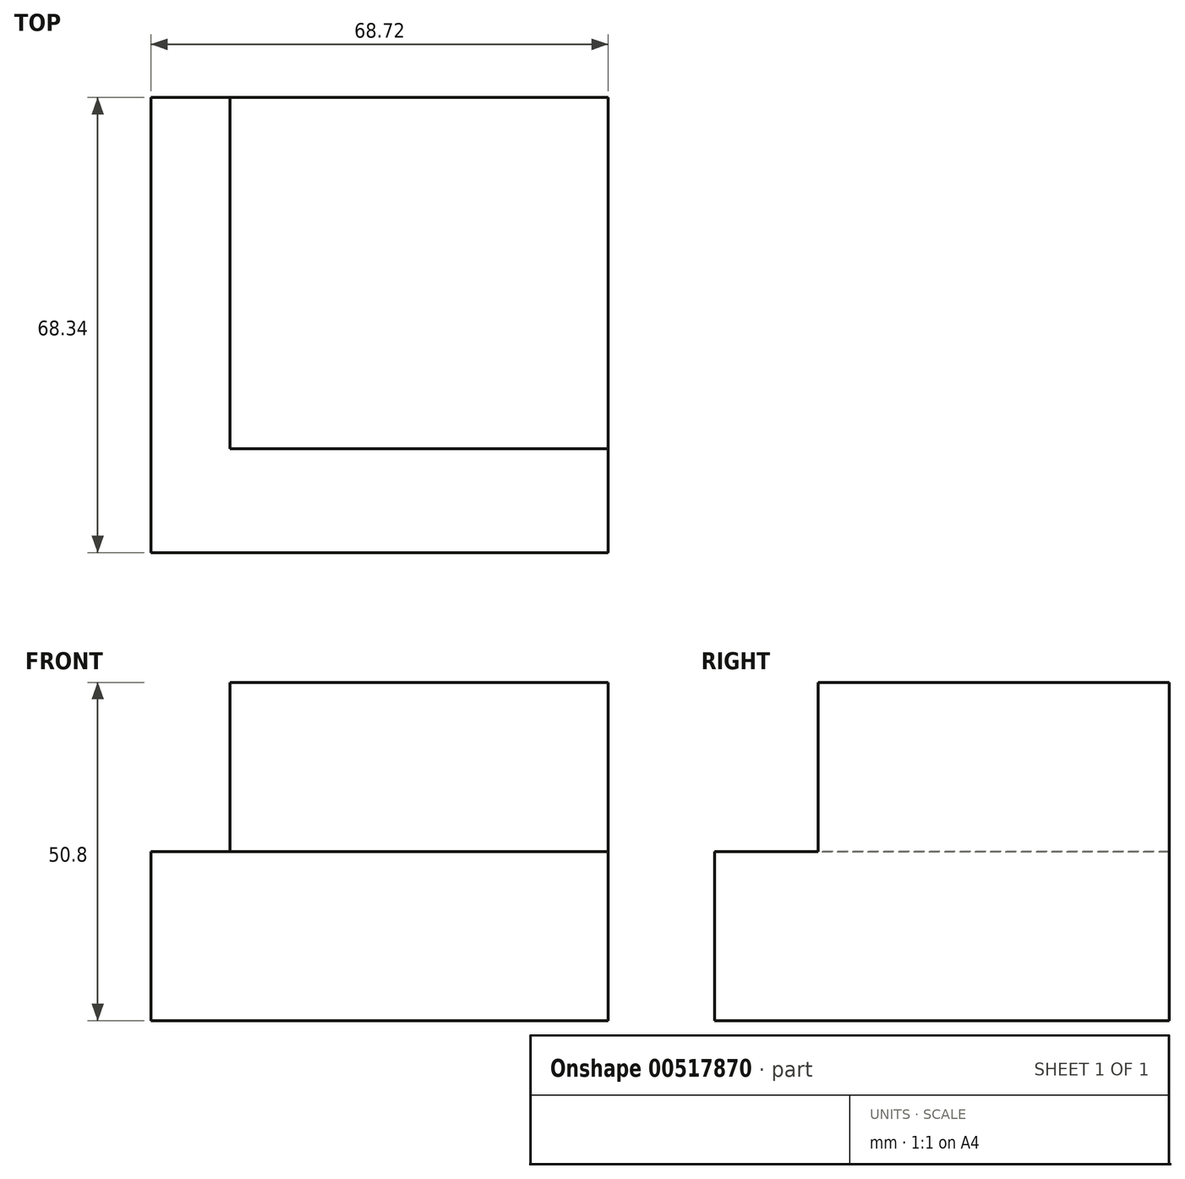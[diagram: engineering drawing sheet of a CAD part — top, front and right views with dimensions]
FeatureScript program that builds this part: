
annotation { "Feature Type Name" : "Feature", "Feature Type Description" : "" }
export const myFeature = defineFeature(function(context is Context, id is Id, definition is map)
    precondition{}
    {
        {
            var Q0;
            Q0=qCreatedBy(makeId("Top.planeOp"),FACE);
            var sketch = newSketch(context, id + "F0", { "sketchPlane" : qUnion([Q0])});
            skLineSegment(sketch, "E0.bottom", {"start": v(0, 0) * mm, "end": v(68.72, 0) * mm});
            skLineSegment(sketch, "E0.top", {"start": v(0, 68.34) * mm, "end": v(68.72, 68.34) * mm});
            skLineSegment(sketch, "E0.left", {"start": v(0, 0) * mm, "end": v(0, 68.34) * mm});
            skLineSegment(sketch, "E0.right", {"start": v(68.72, 0) * mm, "end": v(68.72, 68.34) * mm});
            skSolve(sketch);
        }
        {
            var Q0;
            Q0=makeQuery(id+"F0.imprint","IMPRINT",FACE,{"disambiguationData":[TD([[makeQuery(id+"F0.imprint","IMPRINT",EDGE,{"derivedFrom":sQuery(id+"F0.wireOp",EDGE,"E0.bottom")}),1.0]])]});
            extrude(context, id + "F1", {"entities" : qUnion([Q0]), "depth" : 25.4 * mm, "offsetDistance" : 25.4 * mm});
        }
        {
            var Q0;
            Q0=makeQuery(id+"F1.opExtrude","CAP_FACE",FACE,{"disambiguationData":[OSD([sQuery(id+"F0.wireOp",EDGE,"E0.bottom"),sQuery(id+"F0.wireOp",EDGE,"E0.top"),sQuery(id+"F0.wireOp",EDGE,"E0.left"),sQuery(id+"F0.wireOp",EDGE,"E0.right")])],"isStart":false});
            var sketch = newSketch(context, id + "F2", { "sketchPlane" : qUnion([Q0])});
            skLineSegment(sketch, "E1.bottom", {"start": v(68.72, 68.34) * mm, "end": v(11.88, 68.34) * mm});
            skLineSegment(sketch, "E1.top", {"start": v(68.72, 15.56) * mm, "end": v(11.88, 15.56) * mm});
            skLineSegment(sketch, "E1.left", {"start": v(68.72, 68.34) * mm, "end": v(68.72, 15.56) * mm});
            skLineSegment(sketch, "E1.right", {"start": v(11.88, 68.34) * mm, "end": v(11.88, 15.56) * mm});
            skSolve(sketch);
        }
        {
            var Q0;
            Q0 = qSketchRegion(id + "F2", true);
            extrude(context, id + "F3", {"entities" : qUnion([Q0]), "operationType" : NewBodyOperationType.ADD, "depth" : 25.4 * mm, "offsetDistance" : 25.4 * mm});
        }
    });
